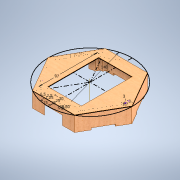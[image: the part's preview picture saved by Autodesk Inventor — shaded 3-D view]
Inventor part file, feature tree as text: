
AUTODESK INVENTOR PART (.ipt)
format: ipt  version: 2020 (Build 240168000, 168)  size: 344,064 bytes
history: native  units: mm
features: extrude x7, sketch x2, pattern_circular x1
ambient origin geometry x8: Origin, YZ Plane, XZ Plane, XY Plane, X Axis, Y Axis, Z Axis, Center Point
bodies: Body1 (feature_tree)
feature tree (10):
  sketch  "Sketch6"  dims[d44=97.0mm d72=6.5mm]
  extrude  "Fronte"  Depth=6.5mm
  extrude  "Esterno"  Depth=0.5mm TaperAngle=0.0deg
  extrude  "Strip"  Depth=15.0mm
  extrude  "Passacavi"  Depth=6.5mm
  extrude  "ScavoStrip"  Depth=30.0mm
  extrude  "ScreenDist0.8"  Depth=2.5mm
  extrude  "SupportoViti"  Depth=2.5mm
  pattern_circular  "RipetizioneSupports"  [2 undecoded]
  sketch  "Sketch7"  dims[d77=140.0mm d85=0.5mm d86=0.0mm d87=15.0mm d88=6.5mm d89=30.0mm d91=2.5mm d92=2.5mm d95=1.25mm d96=25.0mm d97=2.5mm d98=25.0mm d99=135.0deg d100=0.0mm d101=25.0mm d102=0.0mm d103=10.0mm d104=0.0mm d105=3.0mm d106=0.0mm d107=5.0mm d108=0.0mm d111=0.8mm d112=0.0mm d114=1.7mm d115=23.0mm d116=0.0mm d117=3.0mm d118=60.0mm d119=360.0deg d121=3.0mm d123=6.0mm]
note: 2 required parameter values undecoded (feature->parameter linkage not recoverable at this tier; creation-order binding heuristic only, values carry confidence <= 0.55)
